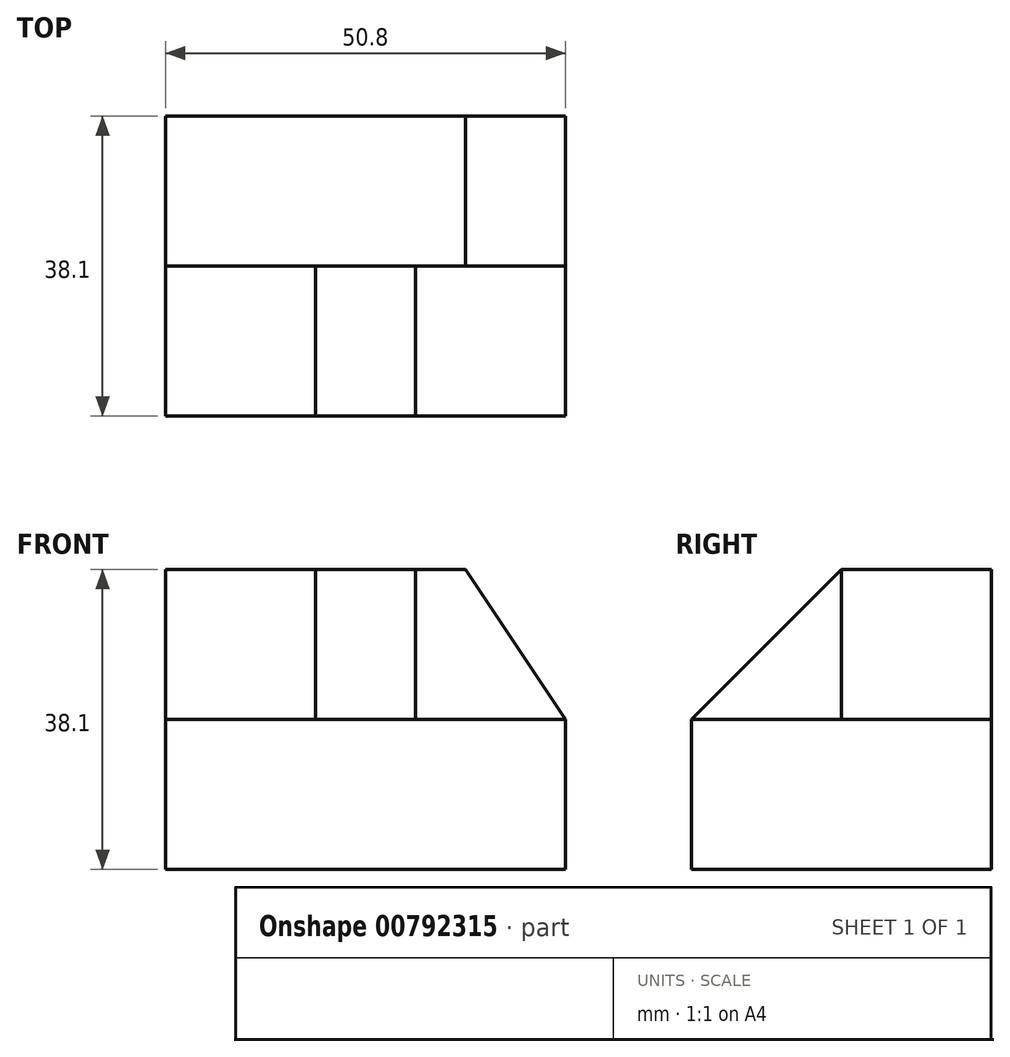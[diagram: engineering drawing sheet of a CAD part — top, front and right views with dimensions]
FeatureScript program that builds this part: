
annotation { "Feature Type Name" : "Feature", "Feature Type Description" : "" }
export const myFeature = defineFeature(function(context is Context, id is Id, definition is map)
    precondition{}
    {
        {
            var Q0;
            Q0=qCreatedBy(makeId("Top.planeOp"),FACE);
            var sketch = newSketch(context, id + "F0", { "sketchPlane" : qUnion([Q0])});
            skLineSegment(sketch, "E0.bottom", {"start": v(0, 0) * mm, "end": v(50.8, 0) * mm});
            skLineSegment(sketch, "E0.top", {"start": v(0, 38.1) * mm, "end": v(50.8, 38.1) * mm});
            skLineSegment(sketch, "E0.left", {"start": v(0, 0) * mm, "end": v(0, 38.1) * mm});
            skLineSegment(sketch, "E0.right", {"start": v(50.8, 0) * mm, "end": v(50.8, 38.1) * mm});
            skSolve(sketch);
        }
        {
            var Q0;
            Q0=qSketchRegion(id+"F0",true);
            extrude(context, id + "F1", {"entities" : qUnion([Q0]), "depth" : 38.1 * mm, "offsetDistance" : 25.4 * mm});
        }
        {
            var Q0;
            Q0=makeQuery(id+"F1.opExtrude","SWEPT_FACE",FACE,{"disambiguationData":[OSD([sQuery(id+"F0.wireOp",EDGE,"E0.left")])]});
            var sketch = newSketch(context, id + "F2", { "sketchPlane" : qUnion([Q0])});
            skLineSegment(sketch, "E1.bottom", {"start": v(0, 38.1) * mm, "end": v(-19.05, 38.1) * mm});
            skLineSegment(sketch, "E1.top", {"start": v(0, 19.05) * mm, "end": v(-19.05, 19.05) * mm});
            skLineSegment(sketch, "E1.left", {"start": v(0, 38.1) * mm, "end": v(0, 19.05) * mm});
            skLineSegment(sketch, "E1.right", {"start": v(-19.05, 38.1) * mm, "end": v(-19.05, 19.05) * mm});
            skSolve(sketch);
        }
        {
            var Q0;
            Q0=makeQuery(id+"F2.imprint","IMPRINT",FACE,{"disambiguationData":[TD([[makeQuery(id+"F2.imprint","IMPRINT",EDGE,{"derivedFrom":sQuery(id+"F2.wireOp",EDGE,"E1.bottom")}),1.0]])]});
            extrude(context, id + "F3", {"entities" : qUnion([Q0]), "operationType" : NewBodyOperationType.REMOVE, "oppositeDirection" : true, "depth" : 19.05 * mm, "offsetDistance" : 25.4 * mm});
        }
        {
            var Q0;
            Q0=makeQuery(id+"F1.opExtrude","SWEPT_FACE",FACE,{"disambiguationData":[OSD([sQuery(id+"F0.wireOp",EDGE,"E0.right")])]});
            var sketch = newSketch(context, id + "F4", { "sketchPlane" : qUnion([Q0])});
            skLineSegment(sketch, "E2.bottom", {"start": v(0, 38.1) * mm, "end": v(19.05, 38.1) * mm});
            skLineSegment(sketch, "E2.top", {"start": v(0, 19.05) * mm, "end": v(19.05, 19.05) * mm});
            skLineSegment(sketch, "E2.left", {"start": v(0, 38.1) * mm, "end": v(0, 19.05) * mm});
            skLineSegment(sketch, "E2.right", {"start": v(19.05, 38.1) * mm, "end": v(19.05, 19.05) * mm});
            skSolve(sketch);
        }
        {
            var Q0;
            Q0=makeQuery(id+"F4.imprint","IMPRINT",FACE,{"disambiguationData":[TD([[makeQuery(id+"F4.imprint","IMPRINT",EDGE,{"derivedFrom":sQuery(id+"F4.wireOp",EDGE,"E2.bottom")}),-1.0]])]});
            extrude(context, id + "F5", {"entities" : qUnion([Q0]), "operationType" : NewBodyOperationType.REMOVE, "oppositeDirection" : true, "depth" : 19.05 * mm, "offsetDistance" : 25.4 * mm});
        }
        {
            var Q0;
            Q0=makeQuery(id+"F5.boolean.opBoolean","COPY",FACE,{"derivedFrom":makeQuery(id+"F5.opExtrude","CAP_FACE",FACE,{"disambiguationData":[OSD([sQuery(id+"F4.wireOp",EDGE,"E2.bottom"),sQuery(id+"F4.wireOp",EDGE,"E2.top"),sQuery(id+"F4.wireOp",EDGE,"E2.left"),sQuery(id+"F4.wireOp",EDGE,"E2.right")])],"isStart":false})});
            var sketch = newSketch(context, id + "F6", { "sketchPlane" : qUnion([Q0])});
            skLineSegment(sketch, "E3", {"start": v(0, 19.05) * mm, "end": v(19.05, 38.1) * mm});
            skSolve(sketch);
        }
        {
            var Q0;
            Q0=makeQuery(id+"F6.imprint","IMPRINT",FACE,{"disambiguationData":[TD([[makeQuery(id+"F6.imprint","IMPRINT",EDGE,{"derivedFrom":sQuery(id+"F6.wireOp",EDGE,"E3")}),1.0]])]});
            extrude(context, id + "F7", {"entities" : qUnion([Q0]), "operationType" : NewBodyOperationType.REMOVE, "endBound" : BoundingType.THROUGH_ALL, "oppositeDirection" : true, "depth" : 25.4 * mm, "offsetDistance" : 25.4 * mm});
        }
        {
            var Q0;
            Q0=makeQuery(id+"F5.boolean.opBoolean","COPY",FACE,{"derivedFrom":makeQuery(id+"F5.opExtrude","SWEPT_FACE",FACE,{"disambiguationData":[OSD([sQuery(id+"F4.wireOp",EDGE,"E2.right")])]})});
            var sketch = newSketch(context, id + "F8", { "sketchPlane" : qUnion([Q0])});
            skLineSegment(sketch, "E4", {"start": v(31.75, 38.1) * mm, "end": v(38.1, 38.1) * mm});
            skLineSegment(sketch, "E5", {"start": v(38.1, 38.1) * mm, "end": v(50.8, 19.05) * mm});
            skSolve(sketch);
        }
        {
            var Q0;
            {var subQ0=sQuery(id+"F8.wireOp",EDGE,"E5");Q0=makeQuery(id+"F8.imprint","IMPRINT",FACE,{"disambiguationData":[TD([[makeQuery(id+"F8.imprint","IMPRINT",EDGE,{"derivedFrom":subQ0}),1.0]])]});}
            extrude(context, id + "F9", {"entities" : qUnion([Q0]), "operationType" : NewBodyOperationType.REMOVE, "endBound" : BoundingType.THROUGH_ALL, "oppositeDirection" : true, "depth" : 25.4 * mm, "offsetDistance" : 25.4 * mm});
        }
    });
